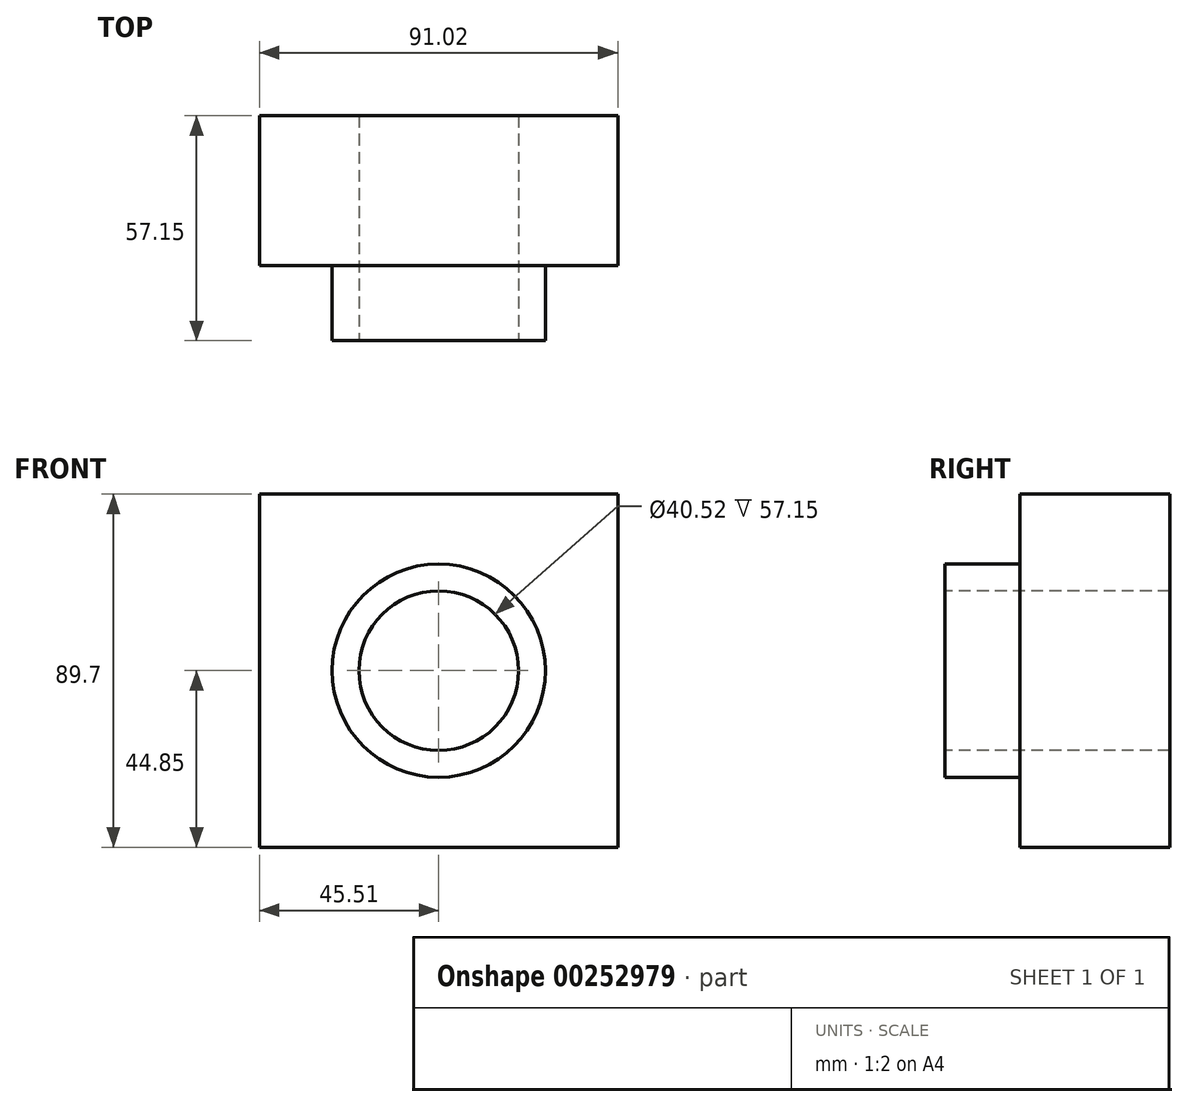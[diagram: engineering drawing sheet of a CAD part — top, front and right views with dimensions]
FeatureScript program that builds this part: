
annotation { "Feature Type Name" : "Feature", "Feature Type Description" : "" }
export const myFeature = defineFeature(function(context is Context, id is Id, definition is map)
    precondition{}
    {
        {
            var Q0;
            Q0=qCreatedBy(makeId("Front.planeOp"),FACE);
            var sketch = newSketch(context, id + "F0", { "sketchPlane" : qUnion([Q0])});
            skLineSegment(sketch, "E0.bottom", {"start": v(45.51, 44.85) * mm, "end": v(-45.51, 44.85) * mm});
            skLineSegment(sketch, "E0.top", {"start": v(45.51, -44.85) * mm, "end": v(-45.51, -44.85) * mm});
            skLineSegment(sketch, "E0.left", {"start": v(45.51, 44.85) * mm, "end": v(45.51, -44.85) * mm});
            skLineSegment(sketch, "E0.right", {"start": v(-45.51, 44.85) * mm, "end": v(-45.51, -44.85) * mm});
            skPoint(sketch, "E0.middle", {"position": v(0, 0) * mm});
            skSolve(sketch);
        }
        {
            var Q0;
            Q0=qSketchRegion(id+"F0",true);
            extrude(context, id + "F1", {"entities" : qUnion([Q0]), "depth" : 38.1 * mm});
        }
        {
            var Q0;
            Q0=makeQuery(id+"F1.opExtrude","CAP_FACE",FACE,{"disambiguationData":[OSD([sQuery(id+"F0.wireOp",EDGE,"E0.bottom"),sQuery(id+"F0.wireOp",EDGE,"E0.top"),sQuery(id+"F0.wireOp",EDGE,"E0.left"),sQuery(id+"F0.wireOp",EDGE,"E0.right")])],"isStart":false});
            var sketch = newSketch(context, id + "F2", { "sketchPlane" : qUnion([Q0])});
            skCircle(sketch, "E1", {"center": v(0, 0) * mm, "radius": 27.1 * mm});
            skSolve(sketch);
        }
        {
            var Q0;
            Q0=qSketchRegion(id+"F2",true);
            var Q1;
            Q1=sQuery(id+"F2.wireOp",EDGE,"E1");
            extrude(context, id + "F3", {"entities" : qUnion([Q0]), "operationType" : NewBodyOperationType.ADD, "surfaceEntities" : qUnion([Q1]), "depth" : 19.05 * mm});
        }
        {
            var Q0;
            Q0=makeQuery(id+"F3.opExtrude","CAP_FACE",FACE,{"disambiguationData":[OSD([sQuery(id+"F2.wireOp",EDGE,"E1")])],"isStart":false});
            var sketch = newSketch(context, id + "F4", { "sketchPlane" : qUnion([Q0])});
            skCircle(sketch, "E2", {"center": v(0, 0) * mm, "radius": 20.26 * mm});
            skSolve(sketch);
        }
        {
            var Q0;
            Q0=qSketchRegion(id+"F4",true);
            extrude(context, id + "F5", {"entities" : qUnion([Q0]), "operationType" : NewBodyOperationType.REMOVE, "endBound" : BoundingType.THROUGH_ALL, "oppositeDirection" : true, "depth" : 25.4 * mm});
        }
    });
